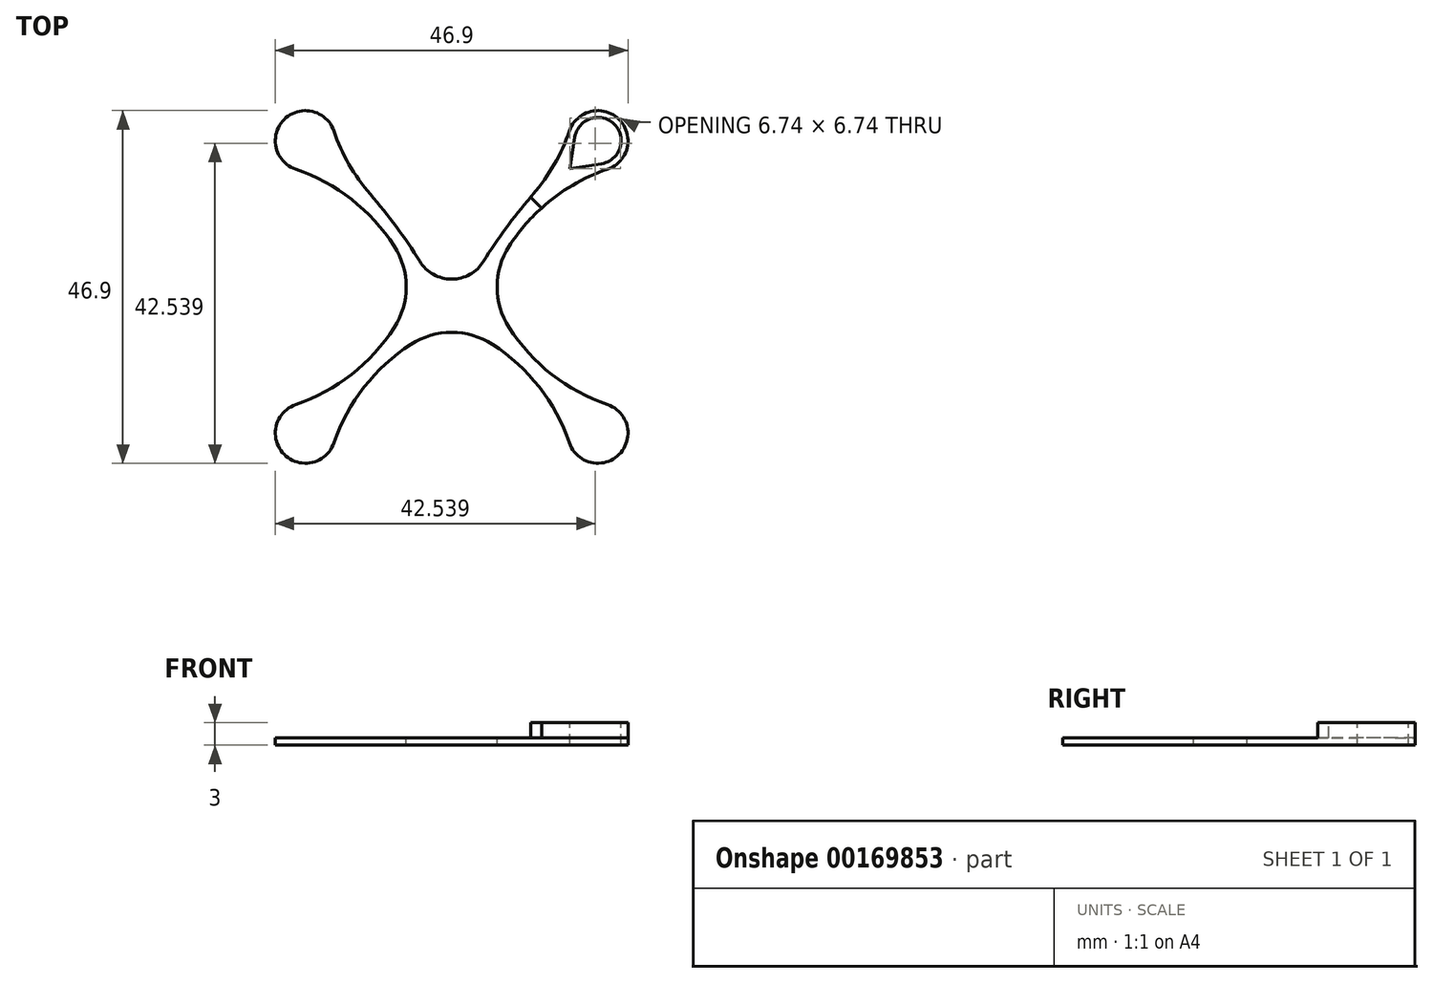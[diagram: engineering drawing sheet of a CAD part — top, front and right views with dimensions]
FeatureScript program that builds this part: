
annotation { "Feature Type Name" : "Feature", "Feature Type Description" : "" }
export const myFeature = defineFeature(function(context is Context, id is Id, definition is map)
    precondition{}
    {
        {
            var Q0;
            Q0=qCreatedBy(makeId("Top.planeOp"),FACE);
            var sketch = newSketch(context, id + "F0", { "sketchPlane" : qUnion([Q0])});
            skLineSegment(sketch, "E0.bottom", {"start": v(50, 50) * mm, "end": v(-50, 50) * mm, "construction": true});
            skLineSegment(sketch, "E0.top", {"start": v(50, -50) * mm, "end": v(-50, -50) * mm, "construction": true});
            skLineSegment(sketch, "E0.left", {"start": v(50, 50) * mm, "end": v(50, -50) * mm, "construction": true});
            skLineSegment(sketch, "E0.right", {"start": v(-50, 50) * mm, "end": v(-50, -50) * mm, "construction": true});
            skPoint(sketch, "E0.middle", {"position": v(0, 0) * mm});
            skSolve(sketch);
        }
        {
            var Q0;
            Q0=qCreatedBy(makeId("Top.planeOp"),FACE);
            var sketch = newSketch(context, id + "F1", { "sketchPlane" : qUnion([Q0])});
            skCircle(sketch, "E1", {"center": v(19.45, 19.45) * mm, "radius": 3.25 * mm, "construction": true});
            skLineSegment(sketch, "E2", {"start": v(0, 0) * mm, "end": v(65.42, 0) * mm, "construction": true});
            skLineSegment(sketch, "E3", {"start": v(0, 0) * mm, "end": v(0, 57) * mm, "construction": true});
            skLineSegment(sketch, "E4.bottom", {"start": v(5, 5) * mm, "end": v(-5, 5) * mm, "construction": true});
            skLineSegment(sketch, "E4.top", {"start": v(5, -5) * mm, "end": v(-5, -5) * mm, "construction": true});
            skLineSegment(sketch, "E4.left", {"start": v(5, 5) * mm, "end": v(5, -5) * mm, "construction": true});
            skLineSegment(sketch, "E4.right", {"start": v(-5, 5) * mm, "end": v(-5, -5) * mm, "construction": true});
            skPoint(sketch, "E4.middle", {"position": v(0, 0) * mm});
            skArc(sketch, "E5", {"start": v(20.74, 15.66) * mm, "mid": v(22.27, 22.27) * mm, "end": v(15.66, 20.74) * mm});
            skLineSegment(sketch, "E6", {"start": v(5, 5) * mm, "end": v(19.45, 19.45) * mm, "construction": true});
            skArc(sketch, "E7", {"start": v(20.74, 15.66) * mm, "mid": v(11.06, 9.65) * mm, "end": v(5, 0) * mm});
            skArc(sketch, "E8", {"start": v(0, 5) * mm, "mid": v(9.65, 11.06) * mm, "end": v(15.66, 20.74) * mm});
            skArc(sketch, "E9.MirrorCS", {"start": v(-20.74, 15.66) * mm, "mid": v(-22.27, 22.27) * mm, "end": v(-15.66, 20.74) * mm});
            skArc(sketch, "E10.MirrorCS", {"start": v(0, 5) * mm, "mid": v(-9.65, 11.06) * mm, "end": v(-15.66, 20.74) * mm});
            skArc(sketch, "E11.MirrorCS", {"start": v(-20.74, 15.66) * mm, "mid": v(-11.06, 9.65) * mm, "end": v(-5, 0) * mm});
            skArc(sketch, "E12.MirrorCS", {"start": v(20.74, -15.66) * mm, "mid": v(22.27, -22.27) * mm, "end": v(15.66, -20.74) * mm});
            skArc(sketch, "E13.MirrorCS", {"start": v(0, -5) * mm, "mid": v(9.65, -11.06) * mm, "end": v(15.66, -20.74) * mm});
            skArc(sketch, "E14.MirrorCS", {"start": v(20.74, -15.66) * mm, "mid": v(11.06, -9.65) * mm, "end": v(5, 0) * mm});
            skArc(sketch, "E15.MirrorCS", {"start": v(-20.74, -15.66) * mm, "mid": v(-22.27, -22.27) * mm, "end": v(-15.66, -20.74) * mm});
            skArc(sketch, "E16.MirrorCS", {"start": v(0, -5) * mm, "mid": v(-9.65, -11.06) * mm, "end": v(-15.66, -20.74) * mm});
            skArc(sketch, "E17.MirrorCS", {"start": v(-20.74, -15.66) * mm, "mid": v(-11.06, -9.65) * mm, "end": v(-5, 0) * mm});
            skLineSegment(sketch, "E18", {"start": v(0, 0) * mm, "end": v(50, 50) * mm, "construction": true});
            skSolve(sketch);
        }
        {
            var Q0;
            Q0=makeQuery(id+"F1.imprint","IMPRINT",FACE,{"disambiguationData":[TD([[makeQuery(id+"F1.imprint","IMPRINT",EDGE,{"derivedFrom":sQuery(id+"F1.wireOp",EDGE,"E5")}),1.0]])]});
            extrude(context, id + "F2", {"entities" : qUnion([Q0]), "depth" : 1 * mm});
        }
        {
            var Q0;
            Q0=makeQuery(id+"F2.opExtrude","CAP_FACE",FACE,{"disambiguationData":[OSD([sQuery(id+"F1.wireOp",EDGE,"E5"),sQuery(id+"F1.wireOp",EDGE,"E7"),sQuery(id+"F1.wireOp",EDGE,"E8"),sQuery(id+"F1.wireOp",EDGE,"E9.MirrorCS"),sQuery(id+"F1.wireOp",EDGE,"E10.MirrorCS"),sQuery(id+"F1.wireOp",EDGE,"E11.MirrorCS"),sQuery(id+"F1.wireOp",EDGE,"E12.MirrorCS"),sQuery(id+"F1.wireOp",EDGE,"E13.MirrorCS"),sQuery(id+"F1.wireOp",EDGE,"E14.MirrorCS"),sQuery(id+"F1.wireOp",EDGE,"E15.MirrorCS"),sQuery(id+"F1.wireOp",EDGE,"E16.MirrorCS"),sQuery(id+"F1.wireOp",EDGE,"E17.MirrorCS")])],"isStart":false});
            var sketch = newSketch(context, id + "F3", { "sketchPlane" : qUnion([Q0])});
            skArc(sketch, "E19", {"start": v(19.93, 16.38) * mm, "mid": v(21.64, 21.64) * mm, "end": v(16.38, 19.93) * mm});
            skLineSegment(sketch, "E20", {"start": v(16.38, 19.93) * mm, "end": v(15.72, 15.72) * mm});
            skLineSegment(sketch, "E21", {"start": v(15.72, 15.72) * mm, "end": v(19.93, 16.38) * mm});
            skSolve(sketch);
        }
        {
            var Q0;
            Q0=makeQuery(id+"F3.imprint","IMPRINT",FACE,{"disambiguationData":[TD([[makeQuery(id+"F3.imprint","IMPRINT",EDGE,{"derivedFrom":sQuery(id+"F3.wireOp",EDGE,"E19")}),1.0]])]});
            extrude(context, id + "F4", {"entities" : qUnion([Q0]), "operationType" : NewBodyOperationType.REMOVE, "endBound" : BoundingType.THROUGH_ALL, "oppositeDirection" : true, "depth" : 25 * mm});
        }
        {
            var Q0;
            Q0=makeQuery(id+"F2.opExtrude","CAP_FACE",FACE,{"disambiguationData":[OSD([sQuery(id+"F1.wireOp",EDGE,"E5"),sQuery(id+"F1.wireOp",EDGE,"E7"),sQuery(id+"F1.wireOp",EDGE,"E8"),sQuery(id+"F1.wireOp",EDGE,"E9.MirrorCS"),sQuery(id+"F1.wireOp",EDGE,"E10.MirrorCS"),sQuery(id+"F1.wireOp",EDGE,"E11.MirrorCS"),sQuery(id+"F1.wireOp",EDGE,"E12.MirrorCS"),sQuery(id+"F1.wireOp",EDGE,"E13.MirrorCS"),sQuery(id+"F1.wireOp",EDGE,"E14.MirrorCS"),sQuery(id+"F1.wireOp",EDGE,"E15.MirrorCS"),sQuery(id+"F1.wireOp",EDGE,"E16.MirrorCS"),sQuery(id+"F1.wireOp",EDGE,"E17.MirrorCS")])],"isStart":false});
            var sketch = newSketch(context, id + "F5", { "sketchPlane" : qUnion([Q0])});
            skArc(sketch, "E22.0", {"start": v(20.74, 15.66) * mm, "mid": v(22.27, 22.27) * mm, "end": v(15.66, 20.74) * mm});
            skLineSegment(sketch, "E22.1", {"start": v(19.93, 16.38) * mm, "end": v(19.93, 16.38) * mm});
            skArc(sketch, "E23.0", {"start": v(20.74, 15.66) * mm, "mid": v(11.06, 9.65) * mm, "end": v(5, 0) * mm});
            skArc(sketch, "E23.1", {"start": v(0, 5) * mm, "mid": v(9.65, 11.06) * mm, "end": v(15.66, 20.74) * mm});
            skLineSegment(sketch, "E24", {"start": v(10.48, 11.94) * mm, "end": v(11.94, 10.48) * mm});
            skLineSegment(sketch, "E25.0", {"start": v(15.72, 15.72) * mm, "end": v(19.93, 16.38) * mm});
            skLineSegment(sketch, "E25.1", {"start": v(16.38, 19.93) * mm, "end": v(15.72, 15.72) * mm});
            skArc(sketch, "E25.2", {"start": v(19.93, 16.38) * mm, "mid": v(21.64, 21.64) * mm, "end": v(16.38, 19.93) * mm});
            skSolve(sketch);
        }
        {
            var Q0;
            Q0=makeQuery(id+"F5.imprint","IMPRINT",FACE,{"disambiguationData":[TD([[makeQuery(id+"F5.imprint","IMPRINT",EDGE,{"derivedFrom":sQuery(id+"F5.wireOp",EDGE,"E22.0")}),1.0]])]});
            extrude(context, id + "F6", {"entities" : qUnion([Q0]), "operationType" : NewBodyOperationType.ADD, "depth" : 2 * mm});
        }
        {
            var Q0;
            Q0=makeQuery(id+"F2.opExtrude","SWEPT_EDGE",EDGE,{"disambiguationData":[OSD([sQuery(id+"F1.wireOp",EDGE,"E7"),sQuery(id+"F1.wireOp",EDGE,"E14.MirrorCS")])]});
            var Q1;
            Q1=makeQuery(id+"F2.opExtrude","SWEPT_EDGE",EDGE,{"disambiguationData":[OSD([sQuery(id+"F1.wireOp",EDGE,"E13.MirrorCS"),sQuery(id+"F1.wireOp",EDGE,"E16.MirrorCS")])]});
            var Q2;
            Q2=makeQuery(id+"F2.opExtrude","SWEPT_EDGE",EDGE,{"disambiguationData":[OSD([sQuery(id+"F1.wireOp",EDGE,"E11.MirrorCS"),sQuery(id+"F1.wireOp",EDGE,"E17.MirrorCS")])]});
            var Q3;
            Q3=makeQuery(id+"F2.opExtrude","SWEPT_EDGE",EDGE,{"disambiguationData":[OSD([sQuery(id+"F1.wireOp",EDGE,"E8"),sQuery(id+"F1.wireOp",EDGE,"E10.MirrorCS")])]});
            fillet(context, id + "F7", {"entities" : qUnion([Q0, Q1, Q2, Q3]), "radius" : 10 * mm, "tangentPropagation" : true, "allowEdgeOverflow" : false});
        }
        {
            var Q0;
            Q0=makeQuery(id+"F2.opExtrude","CAP_FACE",FACE,{"disambiguationData":[OSD([sQuery(id+"F1.wireOp",EDGE,"E5"),sQuery(id+"F1.wireOp",EDGE,"E7"),sQuery(id+"F1.wireOp",EDGE,"E8"),sQuery(id+"F1.wireOp",EDGE,"E9.MirrorCS"),sQuery(id+"F1.wireOp",EDGE,"E10.MirrorCS"),sQuery(id+"F1.wireOp",EDGE,"E11.MirrorCS"),sQuery(id+"F1.wireOp",EDGE,"E12.MirrorCS"),sQuery(id+"F1.wireOp",EDGE,"E13.MirrorCS"),sQuery(id+"F1.wireOp",EDGE,"E14.MirrorCS"),sQuery(id+"F1.wireOp",EDGE,"E15.MirrorCS"),sQuery(id+"F1.wireOp",EDGE,"E16.MirrorCS"),sQuery(id+"F1.wireOp",EDGE,"E17.MirrorCS")])],"isStart":false});
            var sketch = newSketch(context, id + "F8", { "sketchPlane" : qUnion([Q0])});
            skCircle(sketch, "E26", {"center": v(0, 6.04) * mm, "radius": 5 * mm});
            skSolve(sketch);
        }
        {
            var Q0;
            Q0=makeQuery(id+"F8.imprint","IMPRINT",FACE,{"disambiguationData":[TD([[makeQuery(id+"F8.imprint","IMPRINT",EDGE,{"derivedFrom":sQuery(id+"F8.wireOp",EDGE,"DIIG4XLN-6Rqc-FYi3-kq92-WaBtKzsYCf5d")}),1.0]])]});
            var Q1;
            Q1=makeQuery(id+"F8.imprint","IMPRINT",FACE,{"disambiguationData":[TD([[makeQuery(id+"F8.imprint","IMPRINT",EDGE,{"derivedFrom":sQuery(id+"F8.wireOp",EDGE,"E26")}),1.0]])]});
            var Q2;
            Q2=makeQuery(id+"F8.imprint","IMPRINT",FACE,{"disambiguationData":[TD([[makeQuery(id+"F8.imprint","IMPRINT",EDGE,{"derivedFrom":sQuery(id+"F8.wireOp",EDGE,"37fc1325-2a69-4084-99ec-2d94e82ec5910.MirrorC")}),-1.0]])]});
            extrude(context, id + "F9", {"entities" : qUnion([Q0, Q1, Q2]), "operationType" : NewBodyOperationType.REMOVE, "oppositeDirection" : true, "depth" : 25 * mm});
        }
        {
            var Q0;
            Q0=makeQuery(id+"F9.boolean.opBoolean","INTERSECT",EDGE,{"disambiguationData":[OD(1.0)],"derivedFrom":[makeQuery(id+"F7.opFillet","BLEND_FACE",FACE,{"disambiguationData":[OSD([sQuery(id+"F1.wireOp",EDGE,"E8"),sQuery(id+"F1.wireOp",EDGE,"E10.MirrorCS")])]}),makeQuery(id+"F9.opExtrude","SWEPT_FACE",FACE,{"disambiguationData":[OSD([sQuery(id+"F8.wireOp",EDGE,"E26")])]})]});
            var Q1;
            Q1=makeQuery(id+"F9.boolean.opBoolean","INTERSECT",EDGE,{"disambiguationData":[OD(0.0)],"derivedFrom":[makeQuery(id+"F7.opFillet","BLEND_FACE",FACE,{"disambiguationData":[OSD([sQuery(id+"F1.wireOp",EDGE,"E8"),sQuery(id+"F1.wireOp",EDGE,"E10.MirrorCS")])]}),makeQuery(id+"F9.opExtrude","SWEPT_FACE",FACE,{"disambiguationData":[OSD([sQuery(id+"F8.wireOp",EDGE,"E26")])]})]});
            fillet(context, id + "F10", {"entities" : qUnion([Q0, Q1]), "radius" : 70 * mm, "tangentPropagation" : true, "allowEdgeOverflow" : false});
        }
    });
